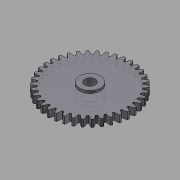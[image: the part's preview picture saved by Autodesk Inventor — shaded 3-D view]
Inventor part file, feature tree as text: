
AUTODESK INVENTOR PART (.ipt)
format: ipt  version: 2015 (Build 190159000, 159)  size: 304,128 bytes
history: native  units: mm (DEFAULTED — no unit token found)
features: sketch x5, extrude x4, plane x3, other x3
ambient origin geometry x8: Origin, YZ Plane, XZ Plane, XY Plane, X Axis, Y Axis, Z Axis, Center Point
bodies: Solid1 (feature_tree)
feature tree (15):
  extrude  "Extrusion1"  Depth=1.7mm TaperAngle=0.0deg
  plane  "Work Plane2"
  plane  "Work Plane8"
  plane  "Work Plane9"
  other  "Spur Gear"
  extrude  "Extrusion2"  Depth=10.0mm TaperAngle=0.0deg
  extrude  "Extrusion3"  Depth=0.826735mm TaperAngle=0.0deg
  extrude  "Extrusion4"  TaperAngle=0.0deg  [1 undecoded]
  sketch  "Sketch1"  dims[d0=20.0mm d1=1.7mm d2=0.0mm]
  sketch  "Sketch2"  dims[d3=19.0mm d4=10.0mm d5=0.0mm]
  other  "Srf1"
  sketch  "Sketch3"  dims[d16=12.0mm d17=0.0mm d34=0.826735mm]
  sketch  "Sketch4"  dims[d39=0.0mm d41=0.0mm]
  sketch  "Sketch5"  dims[d43=12.0mm d46=12.0mm d47=0.0mm d48=0.0mm d49=2.5mm d50=10.0mm d51=0.0mm d52=5.0mm d53=2.5mm d54=1.0mm d55=0.0mm d56=2.5mm d57=5.0mm d58=0.6mm d59=0.0mm]
  other  "Pitch Diameter"
note: 1 required parameter value undecoded (feature->parameter linkage not recoverable at this tier; creation-order binding heuristic only, values carry confidence <= 0.55)
